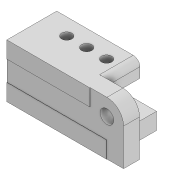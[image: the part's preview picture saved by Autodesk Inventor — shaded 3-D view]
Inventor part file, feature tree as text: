
AUTODESK INVENTOR PART (.ipt)
format: ipt  version: 2022 (Build 260153000, 153)  size: 193,024 bytes
history: native  units: mm
features: extrude x8, sketch x5, projected_geometry x3, pattern_linear x2, fillet x2
ambient origin geometry x8: Origin, YZ Plane, XZ Plane, XY Plane, X Axis, Y Axis, Z Axis, Center Point
bodies: Solid1 (feature_tree)
feature tree (20):
  sketch  "Sketch2"  dims[d0=3.1mm d1=10.0mm]
  extrude  "Extrusion1"  Depth=10.0mm
  extrude  "Extrusion2"  Depth=30.0mm
  pattern_linear  "Rectangular Pattern1"  Count1=3 Spacing1=6.0mm
  pattern_linear  "Rectangular Pattern2"  Count1=2 Spacing1=11.1mm
  sketch  "Sketch3"  dims[d2=5.0mm d3=30.0mm]
  extrude  "Extrusion3"  Depth=5.0mm TaperAngle=0.0deg
  extrude  "Extrusion4"  Depth=5.0mm TaperAngle=0.0deg
  extrude  "Extrusion5"  Depth=2.0mm TaperAngle=0.0deg
  extrude  "Extrusion6"  Depth=2.0mm
  fillet  "Fillet1"  Radius=10.0mm
  extrude  "Extrusion7"  Depth=5.0mm
  extrude  "Extrusion8"  Depth=5.0mm
  fillet  "Fillet2"  Radius=10.0mm
  sketch  "Sketch4"  dims[d4=10.0mm]
  sketch  "Sketch5"  dims[d5=5.0mm d6=0.0mm]
  projected_geometry  "Projected Loop1"
  sketch  "Sketch6"  dims[d7=10.0mm d8=0.0mm d9=30.0mm d11=6.0mm d12=20.0mm d14=11.1mm d18=5.0mm d19=0.0mm d20=5.0mm d21=0.0mm d22=100.0mm d23=0.0mm d28=4.1mm d29=10.0mm d31=5.0mm d32=5.0mm d33=10.0mm d34=0.0mm d35=5.0mm d36=0.1mm d37=0.0mm d38=0.1mm d39=0.0mm d40=2.0mm]
  projected_geometry  "Projected Loop2"
  projected_geometry  "Project Cut Edges1"
